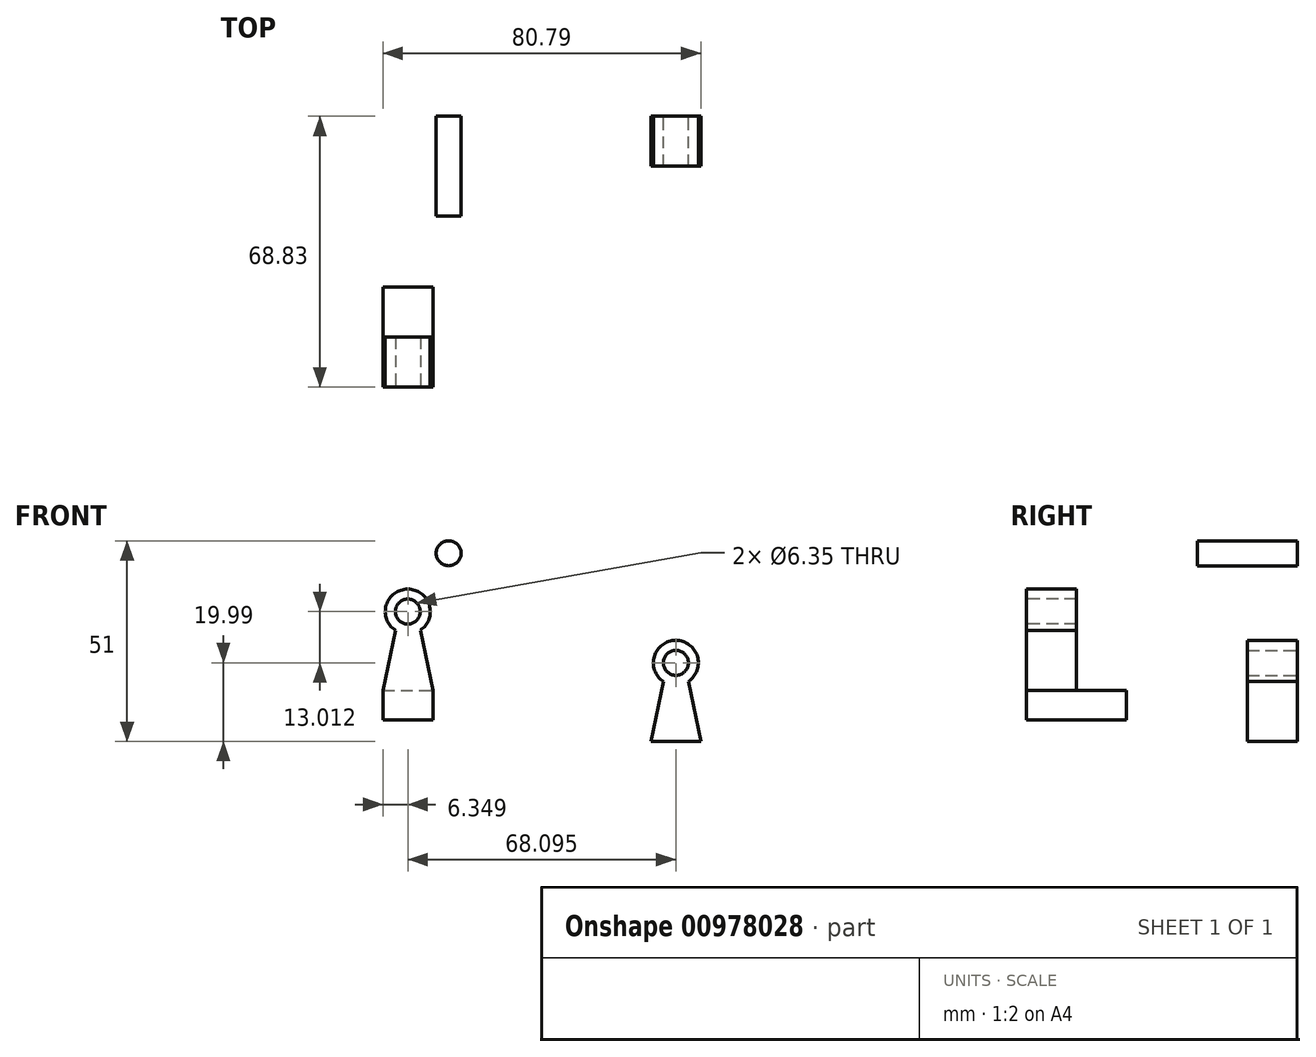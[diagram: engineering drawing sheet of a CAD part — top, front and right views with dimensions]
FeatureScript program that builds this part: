
annotation { "Feature Type Name" : "Feature", "Feature Type Description" : "" }
export const myFeature = defineFeature(function(context is Context, id is Id, definition is map)
    precondition{}
    {
        {
            var Q0;
            Q0=qCreatedBy(makeId("Top.planeOp"),FACE);
            var sketch = newSketch(context, id + "F0", { "sketchPlane" : qUnion([Q0])});
            skLineSegment(sketch, "E0.bottom", {"start": v(-73.65, -43.43) * mm, "end": v(-60.95, -43.43) * mm});
            skLineSegment(sketch, "E0.top", {"start": v(-73.65, -68.83) * mm, "end": v(-60.95, -68.83) * mm});
            skLineSegment(sketch, "E0.left", {"start": v(-73.65, -43.43) * mm, "end": v(-73.65, -68.83) * mm});
            skLineSegment(sketch, "E0.right", {"start": v(-60.95, -43.43) * mm, "end": v(-60.95, -68.83) * mm});
            skSolve(sketch);
        }
        {
            var Q0;
            Q0=makeQuery(id+"F0.imprint","IMPRINT",FACE,{"disambiguationData":[TD([[makeQuery(id+"F0.imprint","IMPRINT",EDGE,{"derivedFrom":sQuery(id+"F0.wireOp",EDGE,"E0.bottom")}),-1.0]])]});
            extrude(context, id + "F1", {"entities" : qUnion([Q0]), "depth" : 7.5 * mm, "offsetDistance" : 25.4 * mm});
        }
        {
            var Q0;
            Q0=makeQuery(id+"F1.opExtrude","SWEPT_FACE",FACE,{"disambiguationData":[OSD([sQuery(id+"F0.wireOp",EDGE,"E0.top")])]});
            var sketch = newSketch(context, id + "F2", { "sketchPlane" : qUnion([Q0])});
            skLineSegment(sketch, "E1", {"start": v(-73.65, 7.5) * mm, "end": v(-67.3, 7.5) * mm, "construction": true});
            skLineSegment(sketch, "E2", {"start": v(-67.3, 7.5) * mm, "end": v(-60.95, 7.5) * mm, "construction": true});
            skLineSegment(sketch, "E3", {"start": v(-73.65, 7.5) * mm, "end": v(-73.65, 22.74) * mm, "construction": true});
            skLineSegment(sketch, "E4", {"start": v(-73.65, 7.5) * mm, "end": v(-70.48, 22.74) * mm});
            skPoint(sketch, "E4.endSnap0", {"position": v(-70.48, 7.5) * mm});
            skLineSegment(sketch, "E5", {"start": v(-60.95, 7.5) * mm, "end": v(-64.13, 22.74) * mm});
            skPoint(sketch, "E5.endSnap0", {"position": v(-64.13, 7.5) * mm});
            skArc(sketch, "E6", {"start": v(-64.13, 22.74) * mm, "mid": v(-67.3, 33.2) * mm, "end": v(-70.48, 22.74) * mm});
            skSolve(sketch);
        }
        {
            var Q0;
            Q0=makeQuery(id+"F2.imprint","IMPRINT",FACE,{"disambiguationData":[TD([[makeQuery(id+"F2.imprint","IMPRINT",EDGE,{"derivedFrom":sQuery(id+"F2.wireOp",EDGE,"E4")}),-1.0]])]});
            extrude(context, id + "F3", {"entities" : qUnion([Q0]), "operationType" : NewBodyOperationType.ADD, "oppositeDirection" : true, "depth" : 12.7 * mm, "offsetDistance" : 25.4 * mm});
        }
        {
            var Q0;
            {var subQ0=sQuery(id+"F0.wireOp",EDGE,"E0.top");Q0=makeQuery(id+"F3.boolean.opBoolean","MERGE",FACE,{"derivedFrom":[makeQuery(id+"F1.opExtrude","SWEPT_FACE",FACE,{"disambiguationData":[OSD([subQ0])]}),makeQuery(id+"F3.opExtrude","CAP_FACE",FACE,{"disambiguationData":[OSD([subQ0,sQuery(id+"F2.wireOp",EDGE,"E4"),sQuery(id+"F2.wireOp",EDGE,"E5"),sQuery(id+"F2.wireOp",EDGE,"E6")])],"isStart":true})]});}
            var sketch = newSketch(context, id + "F4", { "sketchPlane" : qUnion([Q0])});
            skCircle(sketch, "E7", {"center": v(-67.3, 27.5) * mm, "radius": 3.18 * mm});
            skSolve(sketch);
        }
        {
            var Q0;
            Q0=makeQuery(id+"F4.imprint","IMPRINT",FACE,{"disambiguationData":[TD([[makeQuery(id+"F4.imprint","IMPRINT",EDGE,{"derivedFrom":sQuery(id+"F4.wireOp",EDGE,"E7")}),1.0]])]});
            extrude(context, id + "F5", {"entities" : qUnion([Q0]), "operationType" : NewBodyOperationType.REMOVE, "oppositeDirection" : true, "depth" : 25.4 * mm, "offsetDistance" : 25.4 * mm});
        }
        {
            var Q0;
            Q0=qCreatedBy(makeId("Front.planeOp"),FACE);
            var sketch = newSketch(context, id + "F6", { "sketchPlane" : qUnion([Q0])});
            skLineSegment(sketch, "E8", {"start": v(-5.56, -5.51) * mm, "end": v(-5.56, 9.73) * mm, "construction": true});
            skLineSegment(sketch, "E9", {"start": v(-5.56, -5.51) * mm, "end": v(-2.38, 9.73) * mm});
            skLineSegment(sketch, "E10", {"start": v(7.14, -5.51) * mm, "end": v(3.97, 9.73) * mm});
            skArc(sketch, "E11", {"start": v(3.97, 9.73) * mm, "mid": v(0.8, 20.2) * mm, "end": v(-2.38, 9.73) * mm});
            skCircle(sketch, "E12", {"center": v(0.8, 14.48) * mm, "radius": 3.18 * mm});
            skLineSegment(sketch, "E13", {"start": v(-5.56, -5.51) * mm, "end": v(7.14, -5.51) * mm});
            skSolve(sketch);
        }
        {
            var Q0;
            Q0=makeQuery(id+"F6.imprint","IMPRINT",FACE,{"disambiguationData":[TD([[makeQuery(id+"F6.imprint","IMPRINT",EDGE,{"derivedFrom":sQuery(id+"F6.wireOp",EDGE,"E9")}),-1.0]])]});
            extrude(context, id + "F7", {"entities" : qUnion([Q0]), "depth" : 12.7 * mm, "offsetDistance" : 25.4 * mm});
        }
        {
            var Q0;
            Q0=qCreatedBy(makeId("Front.planeOp"),FACE);
            var sketch = newSketch(context, id + "F8", { "sketchPlane" : qUnion([Q0])});
            skCircle(sketch, "E14", {"center": v(-56.92, 42.32) * mm, "radius": 3.18 * mm});
            skSolve(sketch);
        }
        {
            var Q0;
            Q0 = qSketchRegion(id + "F8", true);
            extrude(context, id + "F9", {"entities" : qUnion([Q0]), "depth" : 25.4 * mm, "offsetDistance" : 25.4 * mm});
        }
    });
